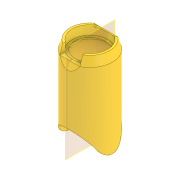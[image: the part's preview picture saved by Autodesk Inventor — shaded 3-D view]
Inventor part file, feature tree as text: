
AUTODESK INVENTOR PART (.ipt)
format: ipt  version: 2020 (Build 240168000, 168)  size: 535,552 bytes
history: native  units: mm
features: sketch x13, extrude x11, revolve x2, plane x2, direct_edit x1, projected_geometry x1, other x1
ambient origin geometry x8: Origin, YZ Plane, XZ Plane, XY Plane, X Axis, Y Axis, Z Axis, Center Point
bodies: Solid1 (feature_tree)
feature tree (31):
  revolve  "Revolution1"  [1 undecoded]
  extrude  "Extrusion1"  Depth=1.1184mm
  extrude  "Extrusion2"  Depth=12.5mm TaperAngle=0.0deg
  extrude  "Extrusion3"  Depth=1.93mm
  extrude  "Extrusion4"  Depth=1.2mm
  plane  "Work Plane1"
  extrude  "Extrusion5"  Depth=24.534mm
  revolve  "Revolution2"  [1 undecoded]
  extrude  "Extrusion6"  Depth=3.99mm
  extrude  "Extrusion7"  Depth=4.6mm
  extrude  "Extrusion8"  Depth=12.5mm TaperAngle=0.0deg
  extrude  "Extrusion9"  Depth=1.239184mm
  direct_edit  "Direct Edit1"
  plane  "Work Plane2"
  extrude  "Extrusion11"  Depth=0.808mm
  extrude  "Extrusion12"  TaperAngle=90.0deg  [1 undecoded]
  sketch  "Sketch1"  dims[d0=10.33mm d10=2.3mm]
  sketch  "Sketch2"  dims[d11=1.2mm d12=1.1184mm]
  sketch  "Sketch3"  dims[d15=90.0deg d18=12.5mm d19=0.0mm]
  sketch  "Sketch4"  dims[d20=1.5mm d21=1.93mm]
  sketch  "Sketch5"  dims[d22=2.5mm d23=1.2mm]
  sketch  "Sketch6"  dims[d24=4.0mm d25=24.534mm]
  projected_geometry  "Projected Loop1"
  sketch  "Sketch7"  dims[d26=1.45mm d27=0.3547mm]
  sketch  "Sketch8"  dims[d28=4.6mm d29=3.99mm]
  sketch  "Sketch9"  dims[d30=12.5mm d31=0.0mm d32=4.6mm]
  sketch  "Sketch10"  dims[d33=0.62mm d34=12.5mm d35=0.0mm]
  sketch  "Sketch11"  dims[d36=0.01mm d37=0.0mm d38=1.239184mm]
  sketch  "Sketch13"  dims[d39=1.51mm d40=0.551mm d41=0.0mm d42=0.0mm d43=0.808mm]
  sketch  "Sketch14"  dims[d44=1.4269mm d45=90.0deg d46=10.0mm d47=46.75mm d48=0.0mm d49=46.75mm d50=0.0mm d51=2.4mm d52=10.0mm d53=10.125mm d54=0.0mm d55=0.0mm d56=15.5mm d57=0.0mm d61=8.0mm d62=10.0mm d63=10.0mm d64=5.5mm d65=14.75mm d66=0.0mm d67=10.25mm d68=0.0mm]
  other  "Scale1"
note: 3 required parameter values undecoded (feature->parameter linkage not recoverable at this tier; creation-order binding heuristic only, values carry confidence <= 0.55)